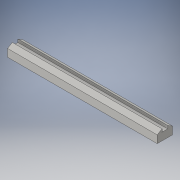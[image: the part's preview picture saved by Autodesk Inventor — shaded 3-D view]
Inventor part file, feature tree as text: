
AUTODESK INVENTOR PART (.ipt)
format: ipt  version: 2016 (Build 200138000, 138)  size: 98,304 bytes
history: native  units: in
note: dims shown in document units (in); Inventor stores cm internally (conversion verified against a paired STEP export)
features: extrude x1, sketch x1
ambient origin geometry x8: Origin, YZ Plane, XZ Plane, XY Plane, X Axis, Y Axis, Z Axis, Center Point
bodies: Solid1 (feature_tree)
feature tree (2):
  extrude  "Extrusion1"  Depth=0.4in
  sketch  "Sketch1"  dims[d0=0.2in d1=0.4in d2=0.075in d3=0.075in d4=0.075in d5=3.937in d6=0.0in]
